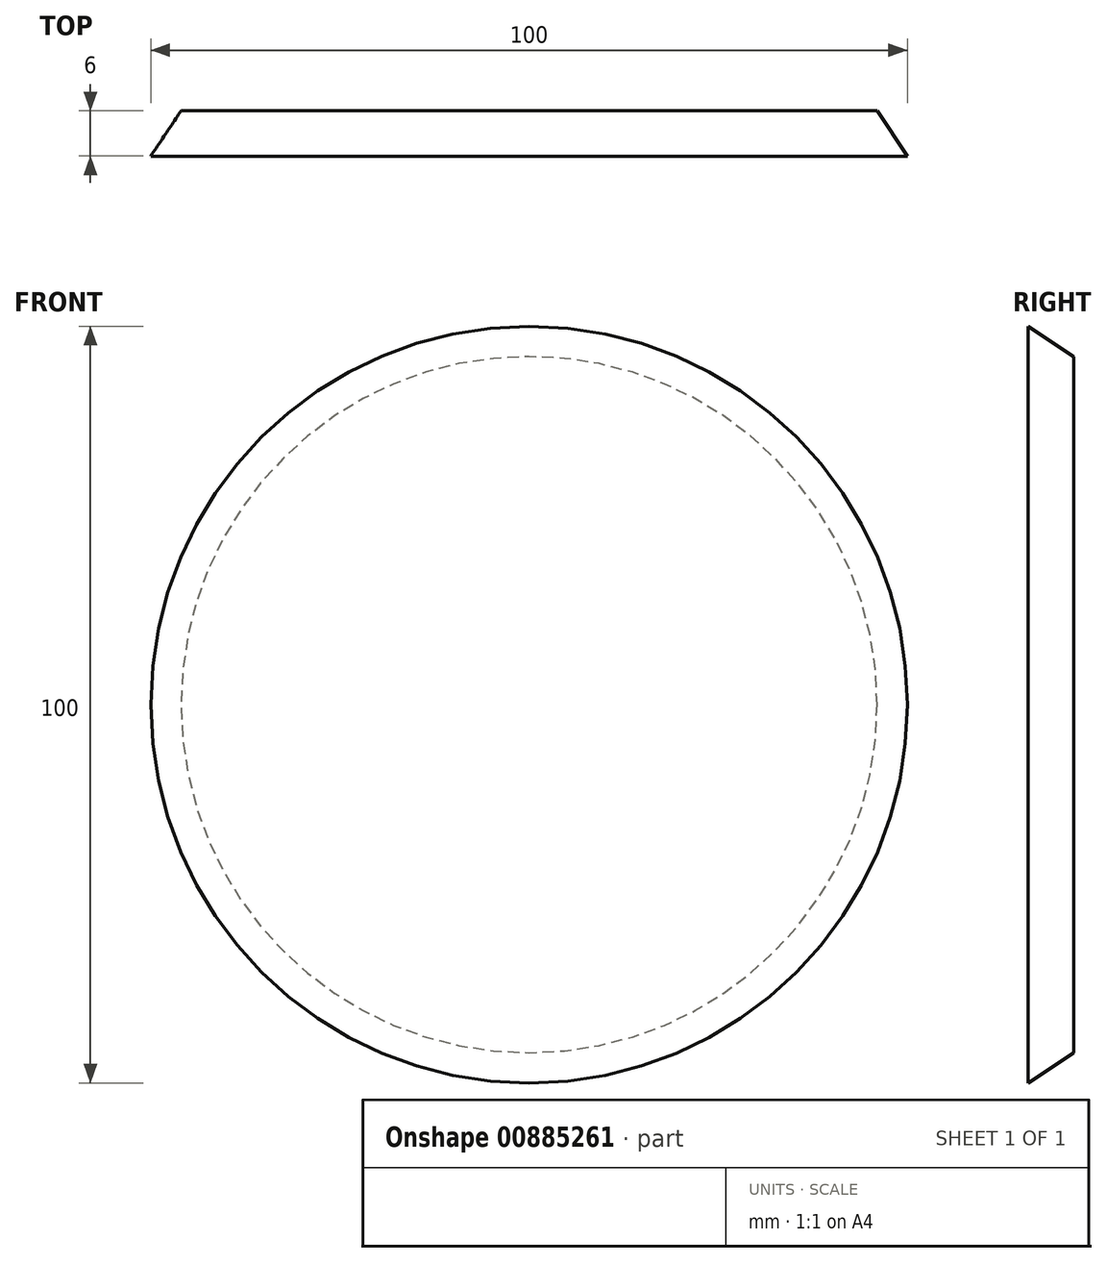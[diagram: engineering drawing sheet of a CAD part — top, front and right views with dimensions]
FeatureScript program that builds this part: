
annotation { "Feature Type Name" : "Feature", "Feature Type Description" : "" }
export const myFeature = defineFeature(function(context is Context, id is Id, definition is map)
    precondition{}
    {
        {
            var Q0;
            Q0=qCreatedBy(makeId("Top.planeOp"),FACE);
            var sketch = newSketch(context, id + "F0", { "sketchPlane" : qUnion([Q0])});
            skLineSegment(sketch, "E0", {"start": v(-65.77, -2.46) * mm, "end": v(34.23, -2.46) * mm});
            skPoint(sketch, "E1", {"position": v(30.23, 3.54) * mm});
            skLineSegment(sketch, "E2", {"start": v(-61.77, 3.54) * mm, "end": v(30.23, 3.54) * mm});
            skLineSegment(sketch, "E3", {"start": v(-61.77, 3.54) * mm, "end": v(-65.77, -2.46) * mm});
            skLineSegment(sketch, "E4", {"start": v(30.23, 3.54) * mm, "end": v(34.23, -2.46) * mm});
            skPoint(sketch, "E5", {"position": v(-15.77, 3.54) * mm});
            skPoint(sketch, "E6", {"position": v(-15.77, -2.46) * mm});
            skLineSegment(sketch, "E7", {"start": v(-15.77, 3.54) * mm, "end": v(-15.77, -2.46) * mm});
            skSolve(sketch);
        }
        {
            var Q0;
            {var subQ0=sQuery(id+"F0.wireOp",EDGE,"E3");Q0=makeQuery(id+"F0.imprint","IMPRINT",FACE,{"disambiguationData":[TD([[makeQuery(id+"F0.imprint","IMPRINT",EDGE,{"derivedFrom":subQ0}),1.0]])]});}
            var Q1;
            Q1=sQuery(id+"F0.wireOp",EDGE,"E7");
            revolve(context, id + "F1", {"surfaceOperationType" : NewSurfaceOperationType.NEW, "entities" : qUnion([Q0]), "axis" : qUnion([Q1]), "revolveType" : RevolveType.FULL});
        }
    });
